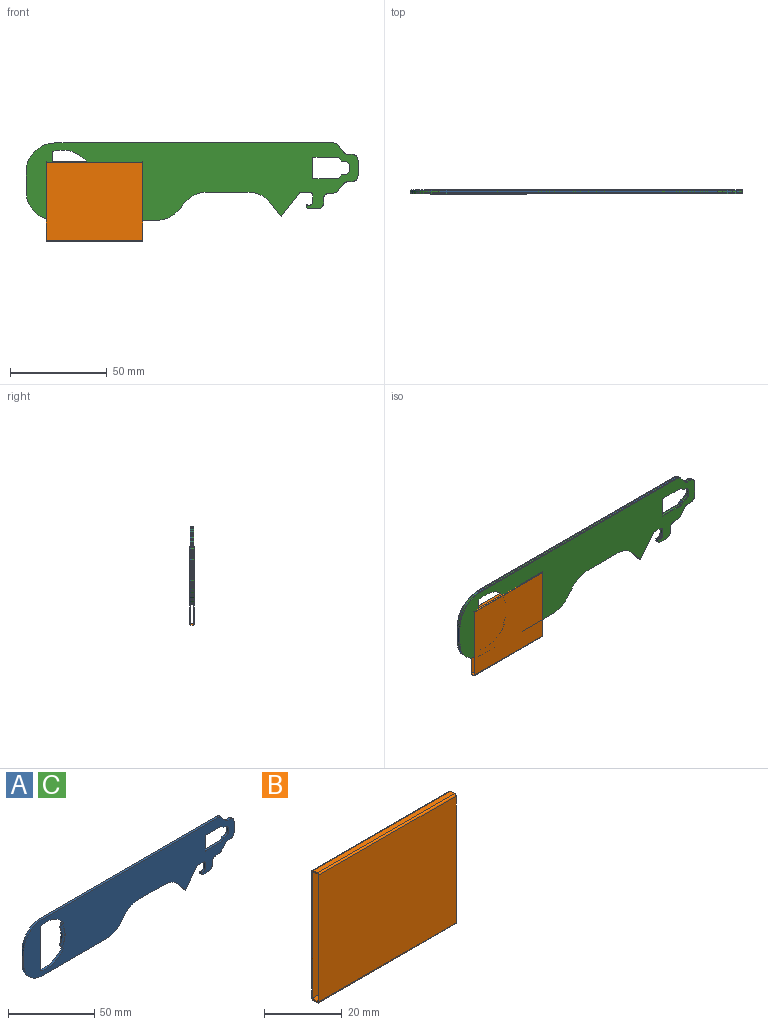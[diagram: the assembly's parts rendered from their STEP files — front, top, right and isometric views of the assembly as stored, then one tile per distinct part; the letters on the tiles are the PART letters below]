
ASSEMBLY  parts=3 mates=1
PART A: 56 faces, bbox 171.9x1.5x40 mm
  f0: cylinder r=13.6mm len=3.2mm, axis (0,-1,0), area 4.7mm2, adj f2,f47,f50,f51,f52,f53,f54,f55
  f1: cylinder r=13.6mm len=3.16mm, axis (0,-1,0), area 4.6mm2, adj f2,f47,f48,f51,f52,f53,f54,f55
  f2: plane 171.86x40mm, normal (0,1,0), area 4790.5mm2, adj f0,f1,f3,f4,f5,f6,f7,f8
  f3: plane 3.64x2.83mm, normal (0.79,0,0.61), area 6.9mm2, adj f2,f4,f46,f47
  f4: cylinder r=3mm len=2.37mm, axis (0,1,0), area 4.1mm2, adj f2,f3,f5,f47
  f5: plane 144.33x1.5mm, normal (0,0,1), area 216.5mm2, adj f2,f4,f6,f47
  f6: cylinder r=15mm len=15mm, axis (0,1,0), area 35.3mm2, adj f2,f5,f7,f47
  f7: plane 10x1.5mm, normal (-1,0,0), area 15mm2, adj f2,f6,f8,f47
  f8: cylinder r=15mm len=15mm, axis (0,1,0), area 35.3mm2, adj f2,f7,f9,f47
  f9: plane 52.65x1.5mm, normal (0,0,-1), area 79mm2, adj f2,f8,f10,f47
  f10: cylinder r=15mm len=11.65mm, axis (0,1,0), area 20mm2, adj f2,f9,f11,f47
  f11: plane 3.48x2.82mm, normal (0.78,0,-0.63), area 6.7mm2, adj f2,f10,f12,f47
  f12: cylinder r=15mm len=11.65mm, axis (0,1,0), area 20mm2, adj f2,f11,f13,f47
  f13: plane 21.12x1.5mm, normal (0,0,-1), area 31.7mm2, adj f2,f12,f14,f47
  f14: cylinder r=15mm len=11.84mm, axis (0,1,0), area 20.5mm2, adj f2,f13,f15,f47
  f15: plane 6.79x5.29mm, normal (-0.79,0,-0.61), area 12.9mm2, adj f2,f14,f16,f47
  f16: plane 12.58x9.79mm, normal (0.79,0,-0.61), area 23.9mm2, adj f2,f15,f17,f47
  f17: plane 4.68x1.5mm, normal (0,0,-1), area 7mm2, adj f2,f16,f18,f47
  f18: cylinder r=2mm len=2.02mm, axis (0,1,0), area 4.7mm2, adj f2,f17,f19,f47
  f19: plane 2.89x1.5mm, normal (-1,0,0.01), area 4.3mm2, adj f2,f18,f20,f47
  f20: cylinder r=2.01mm len=3.21mm, axis (0,1,0), area 6.6mm2, adj f2,f19,f21,f47
  f21: plane 1.5x1.16mm, normal (-1,0,0), area 1.7mm2, adj f2,f20,f22,f47
  f22: cylinder r=1mm len=1.5mm, axis (0,1,0), area 2.4mm2, adj f2,f21,f23,f47
  f23: plane 4.79x1.5mm, normal (0,0,-1), area 7.2mm2, adj f2,f22,f24,f47
  f24: cylinder r=3mm len=3mm, axis (0,1,0), area 7.1mm2, adj f2,f23,f25,f47
  f25: plane 2.17x1.5mm, normal (1,0,0), area 3.3mm2, adj f2,f24,f26,f47
  f26: cylinder r=3mm len=3mm, axis (0,1,0), area 7.1mm2, adj f2,f25,f27,f47
  f27: plane 2.2x1.5mm, normal (0,0,-1), area 3.3mm2, adj f2,f26,f28,f47
  f28: cylinder r=3mm len=2.33mm, axis (0,1,0), area 4mm2, adj f2,f27,f29,f47
  f29: plane 3.73x3.03mm, normal (0.78,0,-0.63), area 7.2mm2, adj f2,f28,f30,f47
  f30: cylinder r=3mm len=2.33mm, axis (0,1,0), area 4mm2, adj f2,f29,f31,f47
  f31: plane 1.92x1.5mm, normal (0,0,-1), area 2.9mm2, adj f2,f30,f32,f47
  f32: cylinder r=3mm len=3mm, axis (0,1,0), area 7.1mm2, adj f2,f31,f33,f47
  f33: plane 8x1.5mm, normal (1,0,0), area 12mm2, adj f2,f32,f34,f47
  f34: cylinder r=3mm len=3mm, axis (0,1,0), area 7.1mm2, adj f2,f33,f35,f47
  f35: plane 1.97x1.5mm, normal (0,0,1), area 2.9mm2, adj f2,f34,f46,f47
  f36: cylinder r=3mm len=3mm, axis (0,1,0), area 7.1mm2, adj f2,f37,f45,f47
  f37: plane 1.5x1mm, normal (-1,0,0), area 1.5mm2, adj f2,f36,f38,f47
  f38: cylinder r=3mm len=3mm, axis (0,1,0), area 7.1mm2, adj f2,f37,f39,f47
  f39: plane 1.5x1.07mm, normal (0,0,1), area 1.6mm2, adj f2,f38,f40,f47
  f40: plane 2x1.62mm, normal (-0.78,0,0.63), area 3.9mm2, adj f2,f39,f41,f47
  f41: plane 13.38x1.5mm, normal (0,0,1), area 20.1mm2, adj f2,f40,f42,f47
  f42: plane 11x1.5mm, normal (1,0,0), area 16.5mm2, adj f2,f41,f43,f47
  f43: plane 13.44x1.5mm, normal (0,0,-1), area 20.2mm2, adj f2,f42,f44,f47
  f44: plane 2x1.56mm, normal (-0.79,0,-0.61), area 3.8mm2, adj f2,f43,f45,f47
  f45: plane 1.5x1.07mm, normal (0,0,-1), area 1.6mm2, adj f2,f36,f44,f47
  f46: cylinder r=3mm len=2.37mm, axis (0,1,0), area 4.1mm2, adj f2,f3,f35,f47
  f47: plane 171.86x40mm, normal (0,-1,0), area 4790.5mm2, adj f0,f1,f3,f4,f5,f6,f7,f8
  f48: cylinder r=16.48mm len=18.58mm, axis (0,-1,0), area 31.7mm2, adj f1,f2,f47,f49
  f49: plane 31.47x1.5mm, normal (1,0,0), area 47.2mm2, adj f2,f47,f48,f50
  f50: cylinder r=16.48mm len=18.58mm, axis (0,-1,0), area 31.7mm2, adj f0,f2,f47,f49
  f51: cylinder r=15mm len=15.99mm, axis (0,-1,0), area 4.2mm2, adj f0,f1,f47,f52
  f52: plane 15.99x3.51mm, normal (0,-1,0), area 30.1mm2, adj f0,f1,f51,f55
  f53: cylinder r=15mm len=15.99mm, axis (0,1,0), area 4.2mm2, adj f0,f1,f2,f54
  f54: plane 15.99x3.51mm, normal (0,1,0), area 30.1mm2, adj f0,f1,f53,f55
  f55: cylinder r=13.25mm len=12.04mm, axis (0,1,0), area 12.5mm2, adj f0,f1,f52,f54
PART B: 14 faces, bbox 50x2.5x41 mm
  f0: cylinder r=0.5mm len=50mm, axis (1,0,0), area 39.3mm2, adj f1,f7,f8,f9
  f1: plane 50x40mm, normal (0,-1,0), area 2000mm2, adj f0,f2,f8,f9
  f2: cylinder r=0.5mm len=50mm, axis (1,0,0), area 39.3mm2, adj f1,f3,f8,f9
  f3: plane 50x1.5mm, normal (0,0,-1), area 75mm2, adj f2,f4,f8,f9
  f4: cylinder r=0.5mm len=50mm, axis (1,0,0), area 39.3mm2, adj f3,f5,f8,f9
  f5: plane 50x40mm, normal (0,1,0), area 2000mm2, adj f4,f6,f8,f9
  f6: cylinder r=0.5mm len=50mm, axis (1,0,0), area 39.3mm2, adj f5,f7,f8,f9
  f7: plane 50x1.5mm, normal (0,0,1), area 75mm2, adj f0,f6,f8,f9
  f8: plane 41x2.5mm, normal (-1,0,0), area 22.3mm2, adj f0,f1,f2,f3,f4,f5,f6,f7
  f9: plane 41x2.5mm, normal (1,0,0), area 22.3mm2, adj f0,f1,f2,f3,f4,f5,f6,f7
  f10: plane 50x2mm, normal (0,0,1), area 100mm2, adj f8,f9,f11,f13
  f11: plane 50x40mm, normal (0,-1,0), area 2000mm2, adj f8,f9,f10,f12
  f12: plane 50x2mm, normal (0,0,-1), area 100mm2, adj f8,f9,f11,f13
  f13: plane 50x40mm, normal (0,1,0), area 2000mm2, adj f8,f9,f10,f12
PART C: same geometry as A
PLACE A t=(5.02,-7.86,5.58)mm
PLACE B t=(-81.08,-8.86,5.71)mm
PLACE C t=(5.02,-8.36,5.58)mm
MATE planar B.f13 <-> C.f47  axis (0,1,0) through (-106.08,-9.86,5.71)mm
